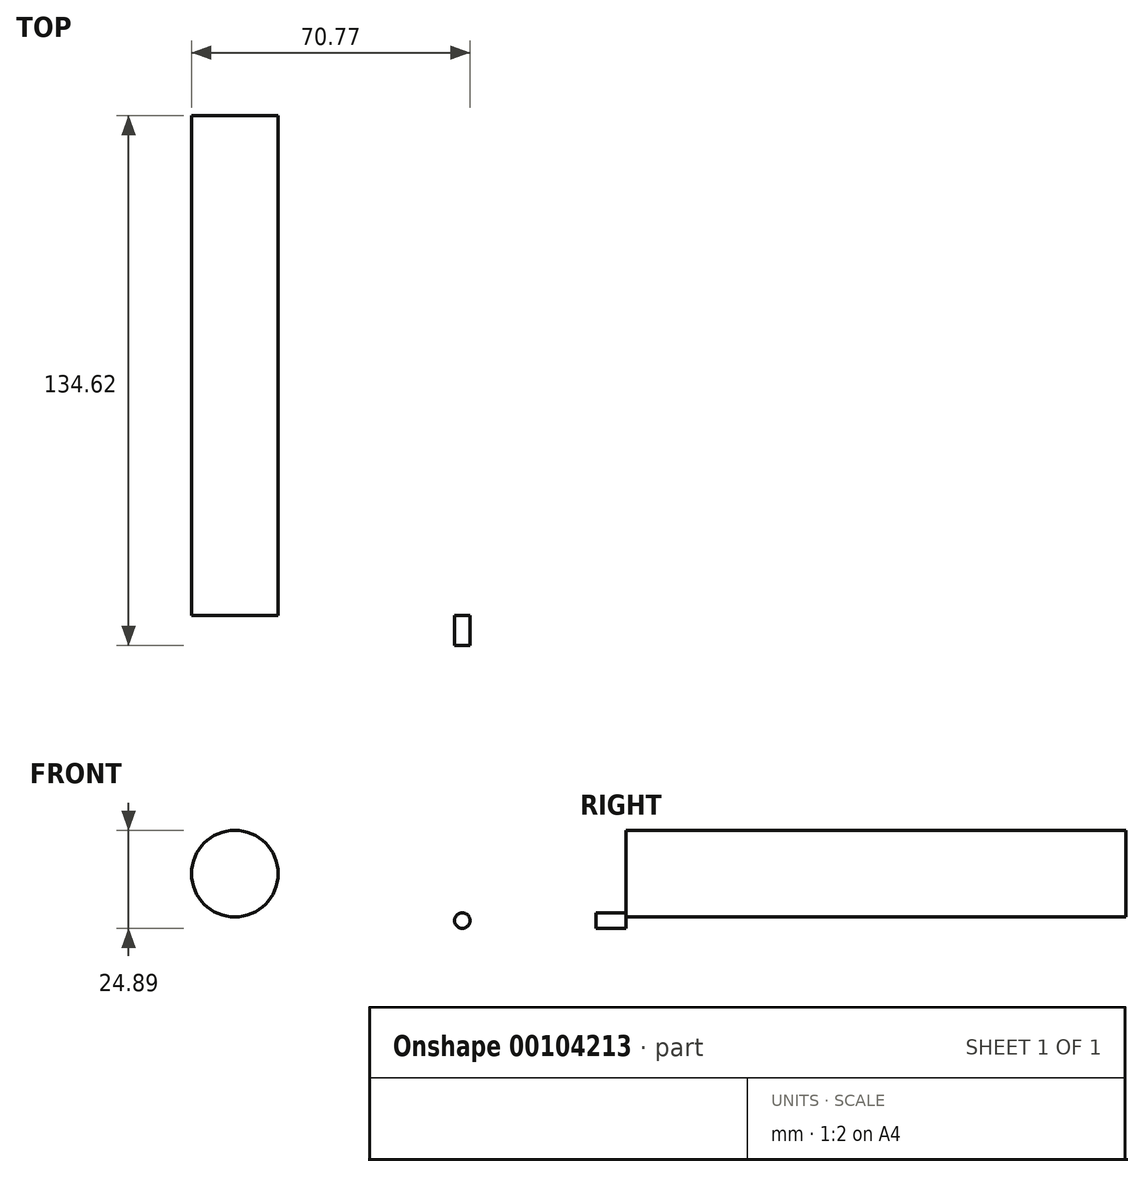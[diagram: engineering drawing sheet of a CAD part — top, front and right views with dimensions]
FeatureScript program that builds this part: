
annotation { "Feature Type Name" : "Feature", "Feature Type Description" : "" }
export const myFeature = defineFeature(function(context is Context, id is Id, definition is map)
    precondition{}
    {
        {
            var Q0;
            Q0=qCreatedBy(makeId("Front.planeOp"),FACE);
            var sketch = newSketch(context, id + "F0", { "sketchPlane" : qUnion([Q0])});
            skCircle(sketch, "E0", {"center": v(-17.28, 12.07) * mm, "radius": 11 * mm});
            skCircle(sketch, "E1", {"center": v(40.53, 0.15) * mm, "radius": 1.97 * mm});
            skSolve(sketch);
        }
        {
            var Q0;
            Q0=makeQuery(id+"F0.imprint","IMPRINT",FACE,{"disambiguationData":[TD([[makeQuery(id+"F0.imprint","IMPRINT",EDGE,{"derivedFrom":sQuery(id+"F0.wireOp",EDGE,"E0")}),1.0]])]});
            extrude(context, id + "F1", {"entities" : qUnion([Q0]), "oppositeDirection" : true, "depth" : 127 * mm});
        }
        {
            var Q0;
            Q0=makeQuery(id+"F0.imprint","IMPRINT",FACE,{"disambiguationData":[TD([[makeQuery(id+"F0.imprint","IMPRINT",EDGE,{"derivedFrom":sQuery(id+"F0.wireOp",EDGE,"E1")}),1.0]])]});
            extrude(context, id + "F2", {"entities" : qUnion([Q0]), "depth" : 7.62 * mm});
        }
    });
